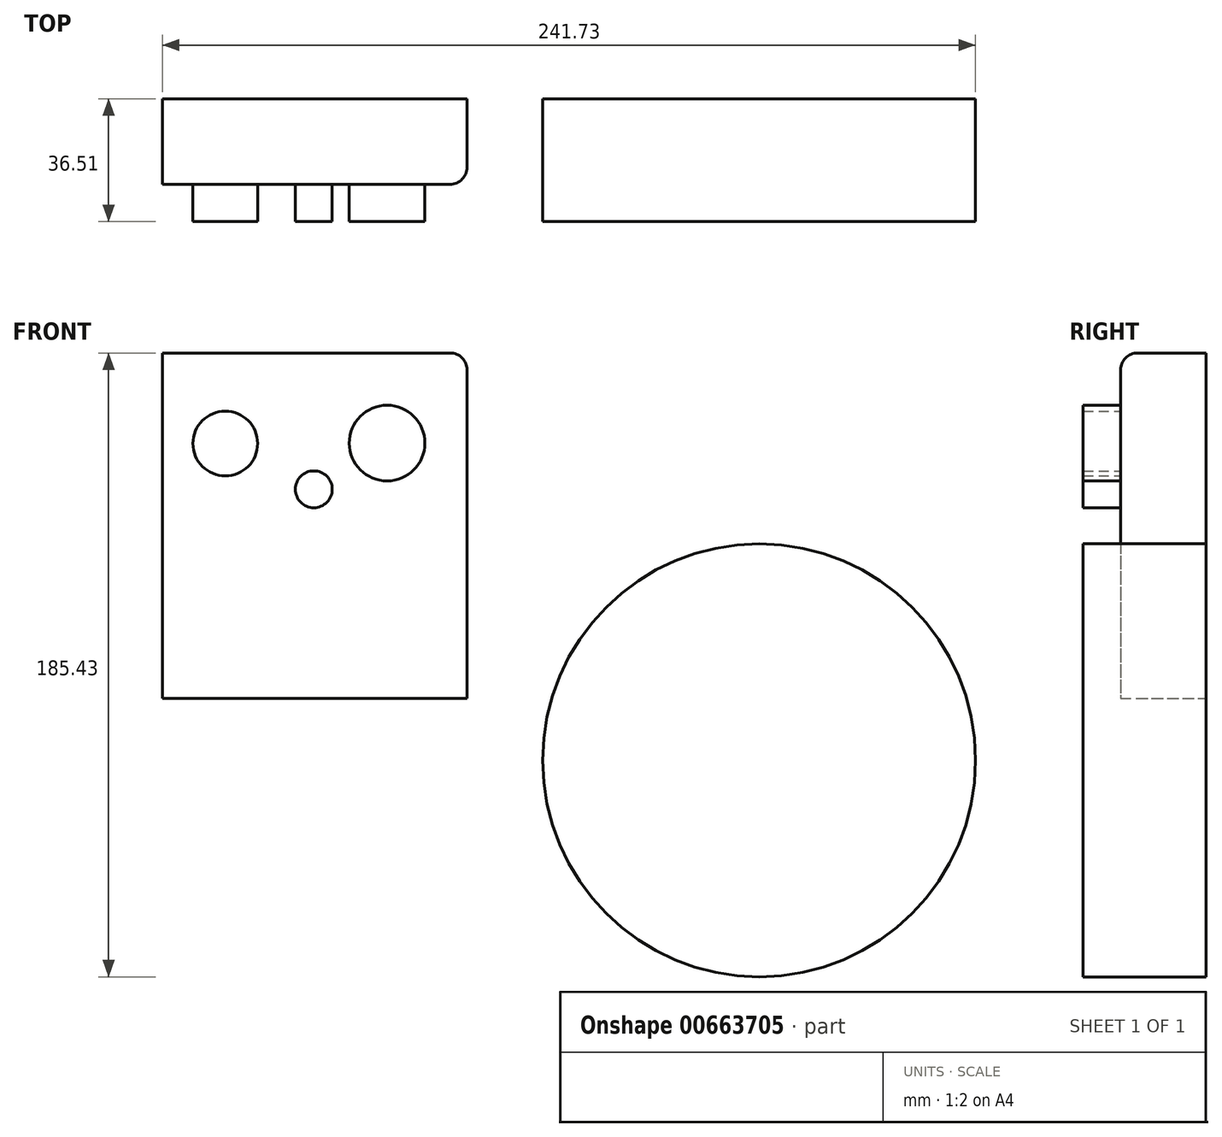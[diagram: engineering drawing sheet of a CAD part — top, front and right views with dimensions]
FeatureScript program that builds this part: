
annotation { "Feature Type Name" : "Feature", "Feature Type Description" : "" }
export const myFeature = defineFeature(function(context is Context, id is Id, definition is map)
    precondition{}
    {
        {
            var Q0;
            Q0=qCreatedBy(makeId("Front.planeOp"),FACE);
            var sketch = newSketch(context, id + "F0", { "sketchPlane" : qUnion([Q0])});
            skLineSegment(sketch, "E0.bottom", {"start": v(-44.99, 40.53) * mm, "end": v(45.58, 40.53) * mm});
            skLineSegment(sketch, "E0.top", {"start": v(-44.99, -62.1) * mm, "end": v(45.58, -62.1) * mm});
            skLineSegment(sketch, "E0.left", {"start": v(-44.99, 40.53) * mm, "end": v(-44.99, -62.1) * mm});
            skLineSegment(sketch, "E0.right", {"start": v(45.58, 40.53) * mm, "end": v(45.58, -62.1) * mm});
            skSolve(sketch);
        }
        {
            var Q0;
            Q0 = qSketchRegion(id + "F0", true);
            extrude(context, id + "F1", {"entities" : qUnion([Q0]), "depth" : 25.4 * mm, "offsetDistance" : 25.4 * mm});
        }
        {
            var Q0;
            Q0=makeQuery(id+"F1.opExtrude","SWEPT_EDGE",EDGE,{"disambiguationData":[OSD([sQuery(id+"F0.wireOp",EDGE,"E0.bottom"),sQuery(id+"F0.wireOp",EDGE,"E0.right")])]});
            fillet(context, id + "F2", {"entities" : qUnion([Q0]), "radius" : 5.08 * mm, "tangentPropagation" : true, "allowEdgeOverflow" : false});
        }
        {
            var Q0;
            Q0=makeQuery(id+"F1.opExtrude","CAP_EDGE",EDGE,{"disambiguationData":[OSD([sQuery(id+"F0.wireOp",EDGE,"E0.bottom")])],"isStart":false});
            fillet(context, id + "F3", {"entities" : qUnion([Q0]), "radius" : 5.08 * mm, "tangentPropagation" : true, "allowEdgeOverflow" : false});
        }
        {
            var Q0;
            Q0=qCreatedBy(makeId("Front.planeOp"),FACE);
            var sketch = newSketch(context, id + "F4", { "sketchPlane" : qUnion([Q0])});
            skCircle(sketch, "E1", {"center": v(-26.32, 13.62) * mm, "radius": 9.63 * mm});
            skCircle(sketch, "E2", {"center": v(21.79, 13.73) * mm, "radius": 11.24 * mm});
            skCircle(sketch, "E3", {"center": v(0, 0) * mm, "radius": 5.48 * mm});
            skCircle(sketch, "E4", {"center": v(132.4, -80.56) * mm, "radius": 64.34 * mm});
            skSolve(sketch);
        }
        {
            var Q0;
            Q0 = qSketchRegion(id + "F4", true);
            extrude(context, id + "F5", {"entities" : qUnion([Q0]), "operationType" : NewBodyOperationType.ADD, "depth" : 36.5 * mm, "offsetDistance" : 25.4 * mm});
        }
    });
